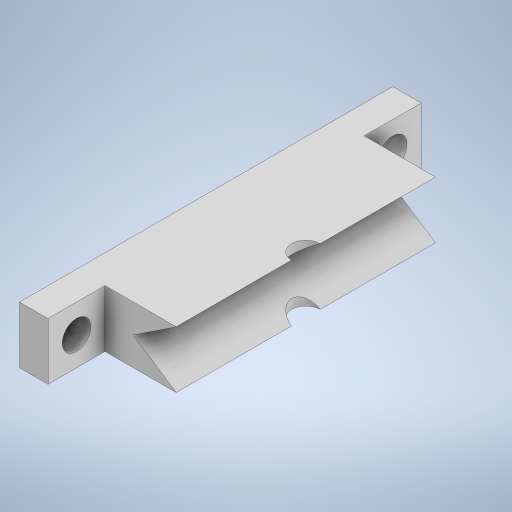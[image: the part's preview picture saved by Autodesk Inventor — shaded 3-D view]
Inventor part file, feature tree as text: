
AUTODESK INVENTOR PART (.ipt)
format: ipt  version: 2023 (Build 270158000, 158)  size: 280,576 bytes
history: native  units: mm
features: extrude x4, sketch x3
ambient origin geometry x8: Origin, YZ Plane, XZ Plane, XY Plane, X Axis, Y Axis, Z Axis, Center Point
bodies: Solid1 (feature_tree)
feature tree (7):
  sketch  "Sketch1"  dims[d0=10.0mm d1=0.0mm d2=5.0mm d3=0.0mm]
  extrude  "Extrusion1"  Depth=5.0mm TaperAngle=0.0deg
  extrude  "Extrusion2"  Depth=10.0mm TaperAngle=0.0deg
  extrude  "Extrusion4"  TaperAngle=0.0deg  [1 undecoded]
  extrude  "Extrusion5"  [1 undecoded]
  sketch  "Sketch2"  dims[d4=15.0mm d7=10.0mm d8=0.0mm]
  sketch  "Sketch3"  dims[d9=5.0mm d10=0.0mm d11=0.0mm]
note: 2 required parameter values undecoded (feature->parameter linkage not recoverable at this tier; creation-order binding heuristic only, values carry confidence <= 0.55)
